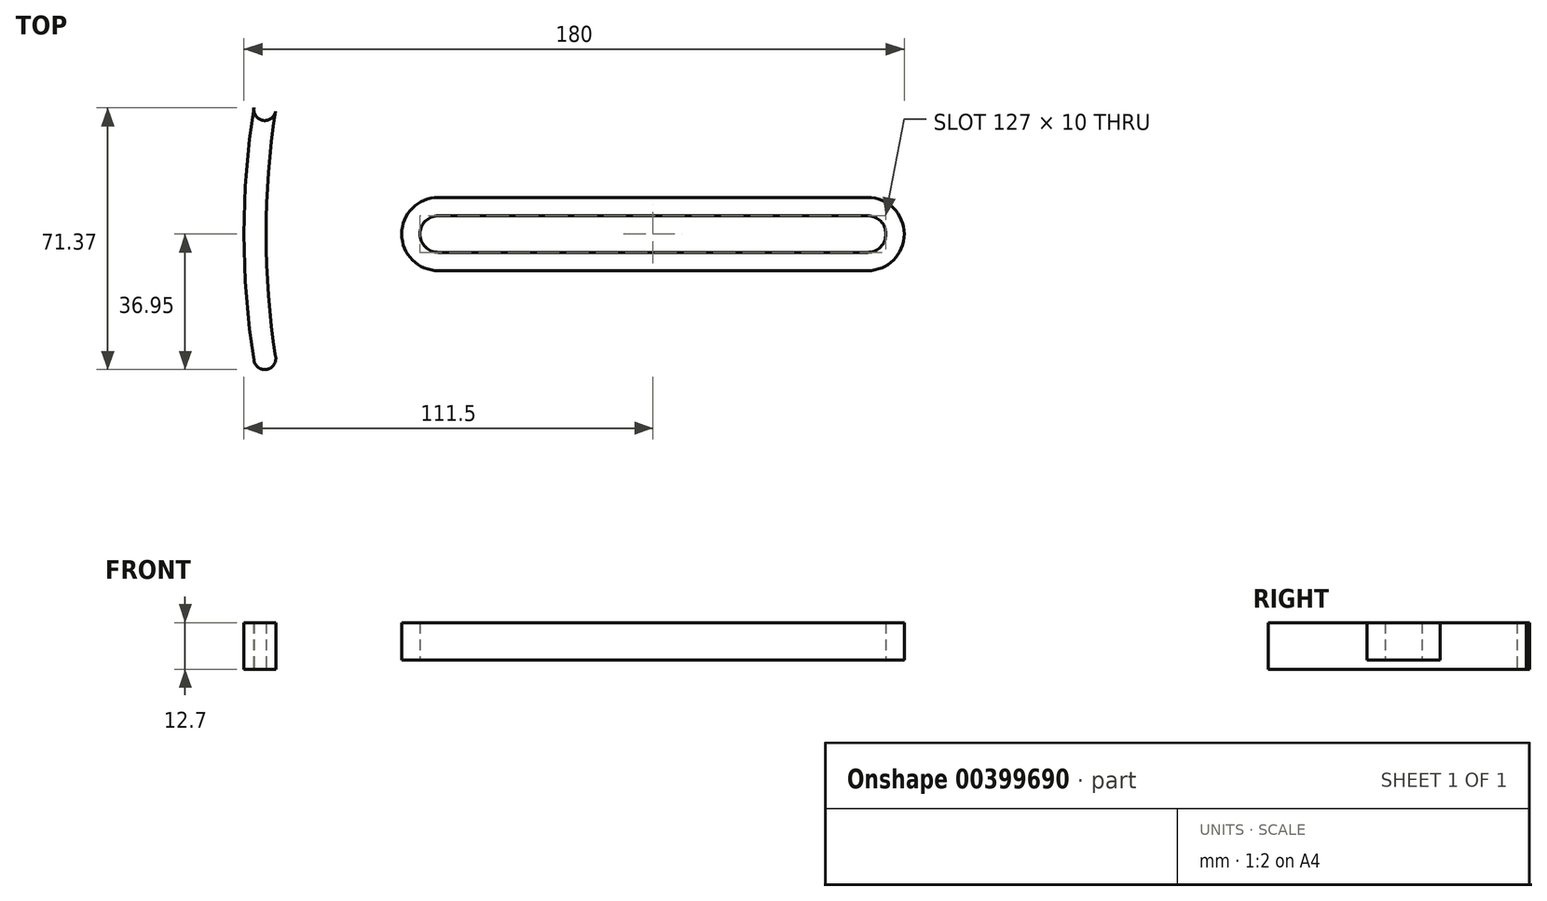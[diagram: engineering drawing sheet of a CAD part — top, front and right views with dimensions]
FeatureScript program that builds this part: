
annotation { "Feature Type Name" : "Feature", "Feature Type Description" : "" }
export const myFeature = defineFeature(function(context is Context, id is Id, definition is map)
    precondition{}
    {
        {
            var Q0;
            Q0=qCreatedBy(makeId("Top.planeOp"),FACE);
            var sketch = newSketch(context, id + "F0", { "sketchPlane" : qUnion([Q0])});
            skLineSegment(sketch, "E0.bottom", {"start": v(-118.5, 52.7) * mm, "end": v(118.5, 52.7) * mm});
            skLineSegment(sketch, "E0.top", {"start": v(-118.5, -52.7) * mm, "end": v(118.5, -52.7) * mm});
            skLineSegment(sketch, "E0.left", {"start": v(-118.5, 52.7) * mm, "end": v(-118.5, -52.7) * mm});
            skLineSegment(sketch, "E0.right", {"start": v(118.5, 52.7) * mm, "end": v(118.5, -52.7) * mm});
            skSolve(sketch);
        }
        {
            var Q0;
            Q0=makeQuery(id+"F0.imprint","IMPRINT",FACE,{"disambiguationData":[TD([[makeQuery(id+"F0.imprint","IMPRINT",EDGE,{"derivedFrom":sQuery(id+"F0.wireOp",EDGE,"E0.bottom")}),-1.0]])]});
            extrude(context, id + "F1", {"entities" : qUnion([Q0]), "depth" : 12.7 * mm});
        }
        {
            var Q0;
            Q0=qCreatedBy(makeId("Top.planeOp"),FACE);
            var sketch = newSketch(context, id + "F2", { "sketchPlane" : qUnion([Q0])});
            skLineSegment(sketch, "E1", {"start": v(-118.5, 0) * mm, "end": v(118.5, 0) * mm, "construction": true});
            skPoint(sketch, "E2", {"position": v(-108.5, 0) * mm});
            skPoint(sketch, "E3", {"position": v(108.5, 0) * mm});
            skCircle(sketch, "E4", {"center": v(108.5, 0) * mm, "radius": 3 * mm});
            skArc(sketch, "E5", {"start": v(-108.5, 0) * mm, "mid": v(-107.48, 21.02) * mm, "end": v(-104.43, 41.84) * mm, "construction": true});
            skPoint(sketch, "E6", {"position": v(-105.5, 0) * mm});
            skPoint(sketch, "E7", {"position": v(-111.5, 0) * mm});
            skArc(sketch, "E8", {"start": v(-105.5, 0) * mm, "mid": v(-104.46, 21.04) * mm, "end": v(-101.36, 41.87) * mm});
            skArc(sketch, "E9", {"start": v(-111.5, 0) * mm, "mid": v(-110.5, 21) * mm, "end": v(-107.49, 41.82) * mm});
            skCircle(sketch, "E10", {"center": v(-105.83, 33.95) * mm, "radius": 3 * mm});
            skLineSegment(sketch, "E11", {"start": v(-105.83, 33.95) * mm, "end": v(108.5, 0) * mm, "construction": true});
            skArc(sketch, "E12.MirrorCS", {"start": v(-105.5, 0) * mm, "mid": v(-104.46, -21.04) * mm, "end": v(-101.36, -41.87) * mm});
            skArc(sketch, "E13.MirrorCS", {"start": v(-111.5, 0) * mm, "mid": v(-110.5, -21) * mm, "end": v(-107.49, -41.82) * mm});
            skCircle(sketch, "E14.MirrorC", {"center": v(-105.83, -33.95) * mm, "radius": 3 * mm});
            skLineSegment(sketch, "E15", {"start": v(0, 52.7) * mm, "end": v(0, -52.7) * mm, "construction": true});
            skLineSegment(sketch, "E16.0", {"start": v(-118.5, 52.7) * mm, "end": v(118.5, 52.7) * mm});
            skLineSegment(sketch, "E17.0", {"start": v(-118.5, 52.7) * mm, "end": v(-118.5, -52.7) * mm});
            skLineSegment(sketch, "E18.0", {"start": v(-118.5, -52.7) * mm, "end": v(118.5, -52.7) * mm});
            skLineSegment(sketch, "E19.0", {"start": v(118.5, 52.7) * mm, "end": v(118.5, -52.7) * mm});
            skArc(sketch, "E20.0", {"start": v(-58.5, 10) * mm, "mid": v(-68.5, 0) * mm, "end": v(-58.5, -10) * mm});
            skLineSegment(sketch, "E20.1", {"start": v(58.5, 10) * mm, "end": v(0, 10) * mm});
            skArc(sketch, "E20.2", {"start": v(58.5, 10) * mm, "mid": v(68.5, 0) * mm, "end": v(58.5, -10) * mm});
            skLineSegment(sketch, "E20.3", {"start": v(-58.5, 10) * mm, "end": v(0, 10) * mm});
            skLineSegment(sketch, "E20.4", {"start": v(58.5, -10) * mm, "end": v(0, -10) * mm});
            skLineSegment(sketch, "E20.5", {"start": v(-58.5, -10) * mm, "end": v(0, -10) * mm});
            skArc(sketch, "E21.0", {"start": v(-58.5, 5) * mm, "mid": v(-63.5, 0) * mm, "end": v(-58.5, -5) * mm});
            skLineSegment(sketch, "E21.1", {"start": v(58.5, -5) * mm, "end": v(0, -5) * mm});
            skArc(sketch, "E21.2", {"start": v(58.5, 5) * mm, "mid": v(63.5, 0) * mm, "end": v(58.5, -5) * mm});
            skLineSegment(sketch, "E21.3", {"start": v(-58.5, -5) * mm, "end": v(0, -5) * mm});
            skLineSegment(sketch, "E21.4", {"start": v(58.5, 5) * mm, "end": v(0, 5) * mm});
            skLineSegment(sketch, "E21.5", {"start": v(-58.5, 5) * mm, "end": v(0, 5) * mm});
            skSolve(sketch);
        }
        {
            var Q0;
            Q0=makeQuery(id+"F2.imprint","IMPRINT",FACE,{"disambiguationData":[TD([[makeQuery(id+"F2.imprint","IMPRINT",EDGE,{"derivedFrom":sQuery(id+"F2.wireOp",EDGE,"E21.0")}),1.0]])]});
            var Q1;
            {var subQ0=sQuery(id+"F2.wireOp",EDGE,"E10");var subQ1=makeQuery(id+"F2.imprint","INTERSECT",VERTEX,{"derivedFrom":[sQuery(id+"F2.wireOp",EDGE,"E8"),subQ0]});Q1=makeQuery(id+"F2.imprint","IMPRINT",FACE,{"disambiguationData":[TD([[makeQuery(id+"F2.imprint","IMPRINT",EDGE,{"disambiguationData":[TD([[subQ1,1.0]])],"derivedFrom":subQ0}),1.0]])]});}
            var Q2;
            {var subQ0=sQuery(id+"F2.wireOp",EDGE,"E12.MirrorCS");var subQ1=sQuery(id+"F2.wireOp",EDGE,"E8");var subQ2=makeQuery(id+"F2.imprint","INTERSECT",VERTEX,{"derivedFrom":[subQ1,subQ0]});Q2=makeQuery(id+"F2.imprint","IMPRINT",FACE,{"disambiguationData":[TD([[makeQuery(id+"F2.imprint","IMPRINT",EDGE,{"disambiguationData":[TD([[subQ2,-1.0]])],"derivedFrom":subQ1}),1.0]])]});}
            var Q3;
            {var subQ0=sQuery(id+"F2.wireOp",EDGE,"E14.MirrorC");var subQ1=makeQuery(id+"F2.imprint","INTERSECT",VERTEX,{"derivedFrom":[sQuery(id+"F2.wireOp",EDGE,"E12.MirrorCS"),subQ0]});Q3=makeQuery(id+"F2.imprint","IMPRINT",FACE,{"disambiguationData":[TD([[makeQuery(id+"F2.imprint","IMPRINT",EDGE,{"disambiguationData":[TD([[subQ1,1.0]])],"derivedFrom":subQ0}),-1.0]])]});}
            var Q4;
            Q4=makeQuery(id+"F2.imprint","IMPRINT",FACE,{"disambiguationData":[TD([[makeQuery(id+"F2.imprint","IMPRINT",EDGE,{"derivedFrom":sQuery(id+"F2.wireOp",EDGE,"E4")}),1.0]])]});
            extrude(context, id + "F3", {"entities" : qUnion([Q0, Q1, Q2, Q3, Q4]), "operationType" : NewBodyOperationType.REMOVE, "endBound" : BoundingType.THROUGH_ALL, "depth" : 25.4 * mm});
        }
        {
            var Q0;
            Q0=makeQuery(id+"F2.imprint","IMPRINT",FACE,{"disambiguationData":[TD([[makeQuery(id+"F2.imprint","IMPRINT",EDGE,{"derivedFrom":sQuery(id+"F2.wireOp",EDGE,"E20.0")}),1.0]])]});
            extrude(context, id + "F4", {"entities" : qUnion([Q0]), "operationType" : NewBodyOperationType.REMOVE, "depth" : 2.54 * mm});
        }
    });
